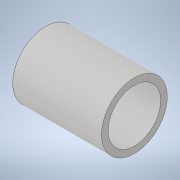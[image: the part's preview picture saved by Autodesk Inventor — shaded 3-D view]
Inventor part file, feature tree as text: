
AUTODESK INVENTOR PART (.ipt)
format: ipt  version: 2021 (Build 250183000, 183)  size: 96,256 bytes
history: native  units: in
note: dims shown in document units (in); Inventor stores cm internally (conversion verified against a paired STEP export)
features: extrude x1, sketch x1
ambient origin geometry x8: Origin, YZ Plane, XZ Plane, XY Plane, X Axis, Y Axis, Z Axis, Center Point
bodies: Solid1 (feature_tree)
feature tree (2):
  extrude  "Extrusion1"  Depth=0.532in
  sketch  "Sketch1"  dims[d0=0.394in d1=0.3153in d2=0.532in d3=0.0in]
